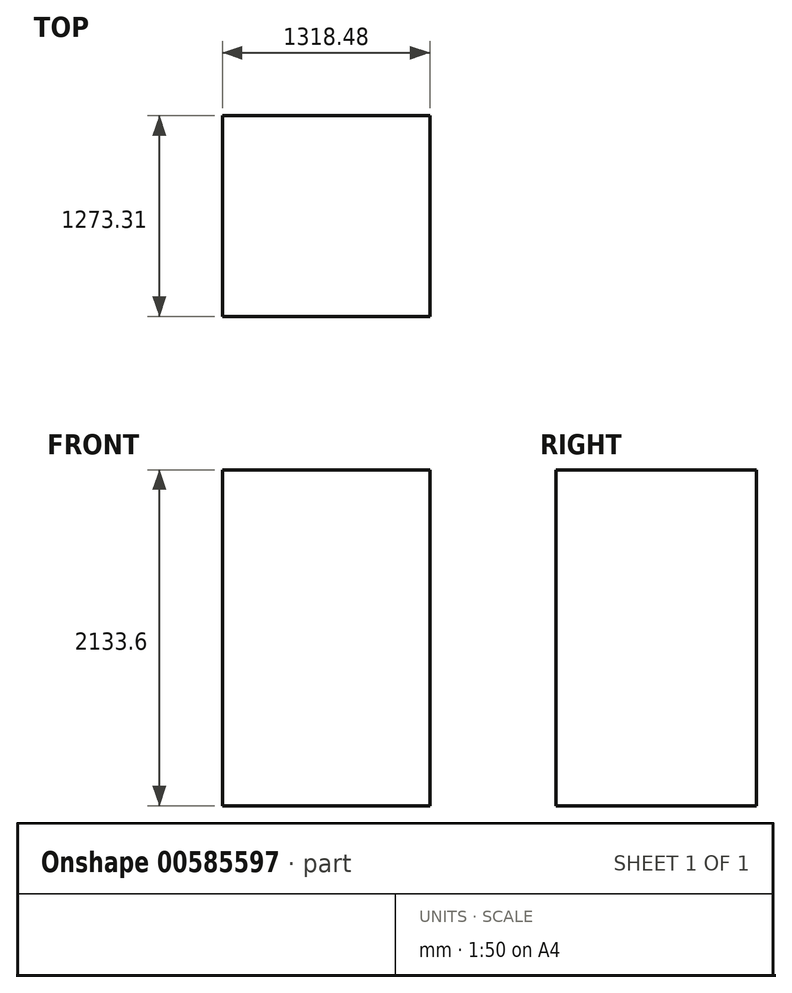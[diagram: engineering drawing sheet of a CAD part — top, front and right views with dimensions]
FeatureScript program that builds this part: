
annotation { "Feature Type Name" : "Feature", "Feature Type Description" : "" }
export const myFeature = defineFeature(function(context is Context, id is Id, definition is map)
    precondition{}
    {
        {
            var Q0;
            Q0=qCreatedBy(makeId("Top.planeOp"),FACE);
            cPlane(context, id + "F0", {"entities" : qUnion([Q0]), "cplaneType" : CPlaneType.OFFSET, "offset" : 1066.8 * mm, "width" : 152.4 * mm, "height" : 152.4 * mm});
        }
        {
            var Q0;
            Q0=qCreatedBy(id+"F0.planeOp",FACE);
            var sketch = newSketch(context, id + "F1", { "sketchPlane" : qUnion([Q0])});
            skLineSegment(sketch, "E0.bottom", {"start": v(618.16, -626.28) * mm, "end": v(-700.32, -626.28) * mm});
            skLineSegment(sketch, "E0.top", {"start": v(618.16, 647.03) * mm, "end": v(-700.32, 647.03) * mm});
            skLineSegment(sketch, "E0.left", {"start": v(618.16, -626.28) * mm, "end": v(618.16, 647.03) * mm});
            skLineSegment(sketch, "E0.right", {"start": v(-700.32, -626.28) * mm, "end": v(-700.32, 647.03) * mm});
            skSolve(sketch);
        }
        {
            var Q0;
            Q0=makeQuery(id+"F1.imprint","IMPRINT",FACE,{"disambiguationData":[TD([[makeQuery(id+"F1.imprint","IMPRINT",EDGE,{"derivedFrom":sQuery(id+"F1.wireOp",EDGE,"E0.bottom")}),-1.0]])]});
            var sketch = newSketch(context, id + "F2", { "sketchPlane" : qUnion([Q0])});
            skSolve(sketch);
        }
        {
            var Q0;
            Q0 = qSketchRegion(id + "F2", true);
            var Q1;
            Q1 = qBodyType(qCreatedBy(id + "F1" ,EDGE), BodyType.WIRE);
            extrude(context, id + "F3", {"entities" : qUnion([Q0]), "bodyType" : ToolBodyType.SURFACE, "surfaceEntities" : qUnion([Q1]), "oppositeDirection" : true, "depth" : 2133.6 * mm, "offsetDistance" : 25.4 * mm});
        }
    });
